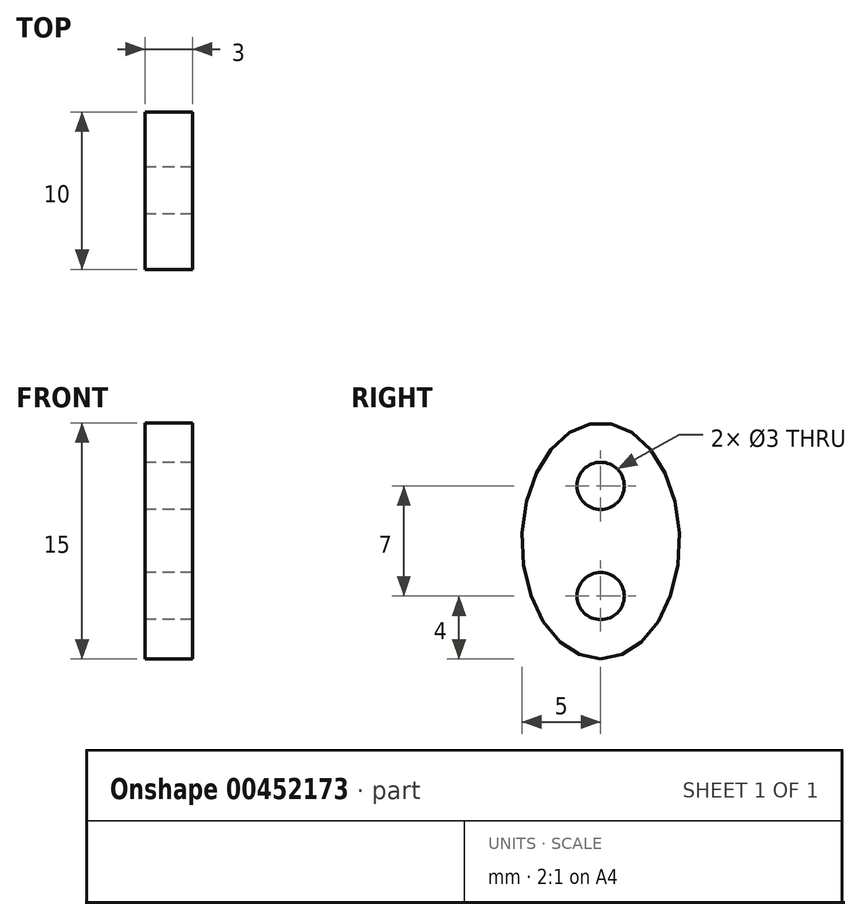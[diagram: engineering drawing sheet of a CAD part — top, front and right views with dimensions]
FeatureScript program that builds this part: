
annotation { "Feature Type Name" : "Feature", "Feature Type Description" : "" }
export const myFeature = defineFeature(function(context is Context, id is Id, definition is map)
    precondition{}
    {
        {
            var Q0;
            Q0=qCreatedBy(makeId("Right.planeOp"),FACE);
            var sketch = newSketch(context, id + "F0", { "sketchPlane" : qUnion([Q0])});
            skEllipse(sketch, "E0", {"center": v(0, 0) * mm, "majorRadius": 7.5 * mm, "minorRadius": 5 * mm, "majorAxis": v(0, -1)});
            skCircle(sketch, "E1", {"center": v(0, 3.5) * mm, "radius": 1.5 * mm});
            skCircle(sketch, "E2", {"center": v(0, -3.5) * mm, "radius": 1.5 * mm});
            skSolve(sketch);
        }
        {
            var Q0;
            Q0=makeQuery(id+"F0.imprint","IMPRINT",FACE,{"disambiguationData":[TD([[makeQuery(id+"F0.imprint","IMPRINT",EDGE,{"derivedFrom":sQuery(id+"F0.wireOp",EDGE,"E0")}),1.0]])]});
            extrude(context, id + "F1", {"entities" : qUnion([Q0]), "depth" : 3 * mm});
        }
    });
